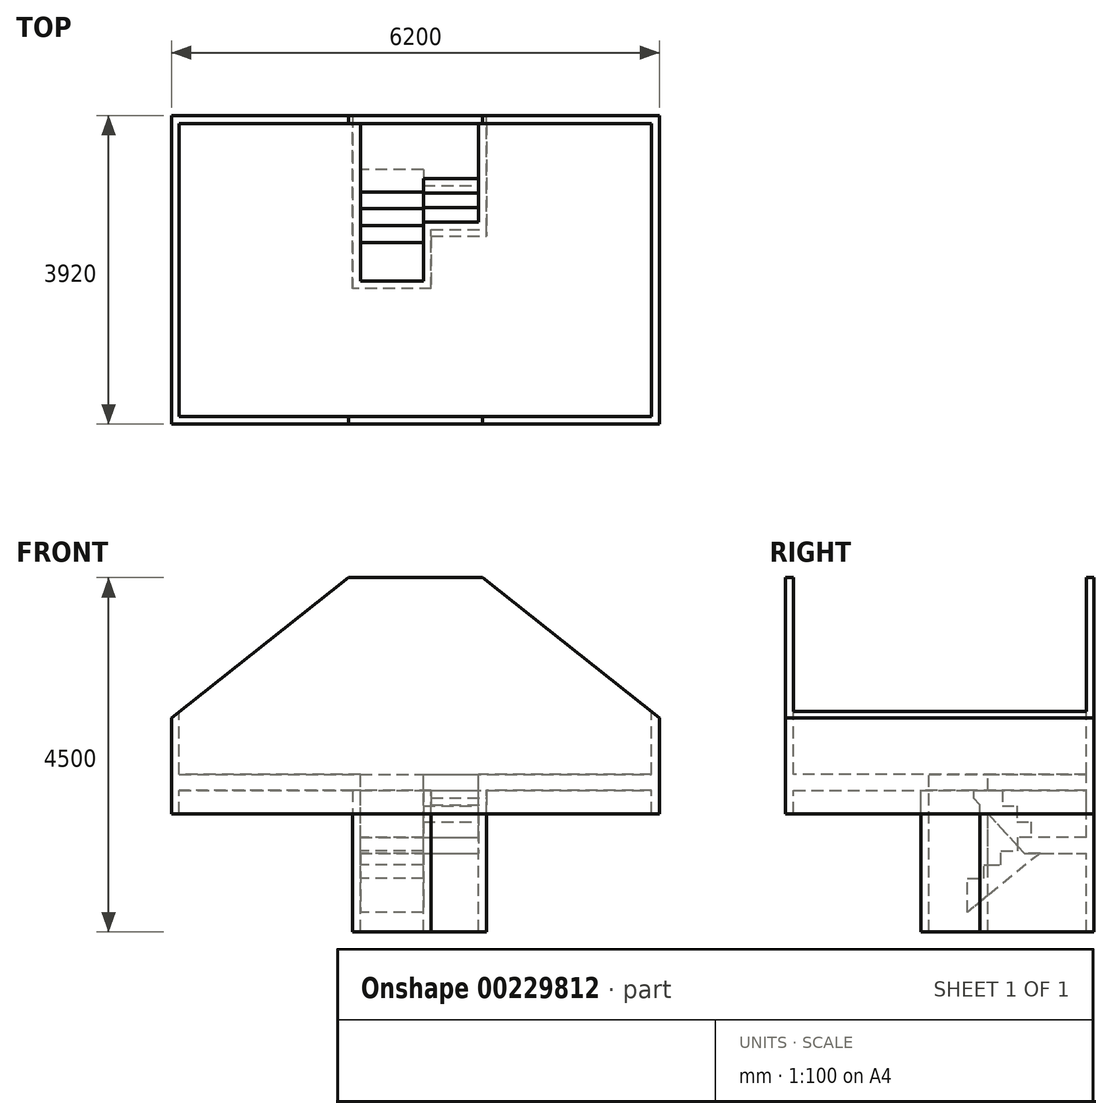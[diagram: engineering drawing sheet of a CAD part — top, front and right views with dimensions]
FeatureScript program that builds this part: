
annotation { "Feature Type Name" : "Feature", "Feature Type Description" : "" }
export const myFeature = defineFeature(function(context is Context, id is Id, definition is map)
    precondition{}
    {
        {
            var Q0;
            Q0=qCreatedBy(makeId("Top.planeOp"),FACE);
            var sketch = newSketch(context, id + "F0", { "sketchPlane" : qUnion([Q0])});
            skLineSegment(sketch, "E0.bottom", {"start": v(0, 0) * mm, "end": v(6000, 0) * mm});
            skLineSegment(sketch, "E0.top", {"start": v(0, -3720) * mm, "end": v(6000, -3720) * mm});
            skLineSegment(sketch, "E0.left", {"start": v(0, 0) * mm, "end": v(0, -3720) * mm});
            skLineSegment(sketch, "E0.right", {"start": v(6000, 0) * mm, "end": v(6000, -3720) * mm});
            skLineSegment(sketch, "E1", {"start": v(2300, 0) * mm, "end": v(2300, -2000) * mm});
            skLineSegment(sketch, "E2", {"start": v(2300, -2000) * mm, "end": v(3100, -2000) * mm});
            skLineSegment(sketch, "E3", {"start": v(3100, -2000) * mm, "end": v(3100, -1250) * mm});
            skLineSegment(sketch, "E4", {"start": v(3100, -1250) * mm, "end": v(3800, -1250) * mm});
            skLineSegment(sketch, "E5", {"start": v(3800, -1250) * mm, "end": v(3800, 0) * mm});
            skSolve(sketch);
        }
        {
            var Q0;
            Q0=qCreatedBy(makeId("Front.planeOp"),FACE);
            var sketch = newSketch(context, id + "F1", { "sketchPlane" : qUnion([Q0])});
            skLineSegment(sketch, "E6", {"start": v(0, 0) * mm, "end": v(0, 800) * mm});
            skLineSegment(sketch, "E7", {"start": v(0, 800) * mm, "end": v(2150, 2500) * mm});
            skLineSegment(sketch, "E8", {"start": v(2150, 2500) * mm, "end": v(3850, 2500) * mm});
            skPoint(sketch, "E9.end.orphan", {"position": v(5620.08, 0) * mm});
            skLineSegment(sketch, "E10.0", {"start": v(0, 0) * mm, "end": v(6000, 0) * mm});
            skLineSegment(sketch, "E11", {"start": v(6000, 0) * mm, "end": v(6000, 800) * mm});
            skLineSegment(sketch, "E12", {"start": v(6000, 800) * mm, "end": v(3850, 2500) * mm});
            skSolve(sketch);
        }
        {
            var Q0;
            Q0 = qSketchRegion(id + "F1", true);
            var sketch = newSketch(context, id + "F2", { "sketchPlane" : qUnion([Q0])});
            skSolve(sketch);
        }
        {
            var Q0;
            Q0=makeQuery(id+"F2.imprint","IMPRINT",FACE,{"disambiguationData":[TD([[makeQuery(id+"F2.imprint","IMPRINT",EDGE,{"derivedFrom":makeQuery(id+"F1.imprint","IMPRINT",EDGE,{"derivedFrom":sQuery(id+"F1.wireOp",EDGE,"E6")})}),-1.0]])]});
            var Q1;
            Q1=sQuery(id+"F0.wireOp",VERTEX,"E0.right.end");
            extrude(context, id + "F3", {"entities" : qUnion([Q0]), "endBound" : BoundingType.UP_TO_VERTEX, "endBoundEntityVertex" : qUnion([Q1]), "depth" : 25 * mm});
        }
        {
            var Q0;
            Q0=makeQuery(id+"F3.opExtrude","SWEPT_FACE",FACE,{"disambiguationData":[OSD([sQuery(id+"F1.wireOp",EDGE,"E12")])]});
            var Q1;
            Q1=makeQuery(id+"F3.opExtrude","SWEPT_FACE",FACE,{"disambiguationData":[OSD([sQuery(id+"F1.wireOp",EDGE,"E8")])]});
            var Q2;
            Q2=makeQuery(id+"F3.opExtrude","SWEPT_FACE",FACE,{"disambiguationData":[OSD([sQuery(id+"F1.wireOp",EDGE,"E7")])]});
            var Q3;
            Q3=makeQuery(id+"F3.opExtrude","SWEPT_FACE",FACE,{"disambiguationData":[OSD([sQuery(id+"F1.wireOp",EDGE,"E10.0")])]});
            var Q4;
            Q4=makeQuery(id+"F3.opExtrude","SWEPT_BODY",BODY,{"disambiguationData":[OSD([sQuery(id+"F1.wireOp",EDGE,"E6"),sQuery(id+"F1.wireOp",EDGE,"E7"),sQuery(id+"F1.wireOp",EDGE,"E8"),sQuery(id+"F1.wireOp",EDGE,"E10.0"),sQuery(id+"F1.wireOp",EDGE,"E11"),sQuery(id+"F1.wireOp",EDGE,"E12")])]});
            shell(context, id + "F4", {"entities" : qUnion([Q0, Q1, Q2, Q3]), "parts" : qUnion([Q4]), "thickness" : 100 * mm, "oppositeDirection" : true});
        }
        {
            var Q0;
            Q0=makeQuery(id+"F3.opExtrude","SWEPT_FACE",FACE,{"disambiguationData":[OSD([sQuery(id+"F1.wireOp",EDGE,"E10.0")])]});
            extrude(context, id + "F5", {"entities" : qUnion([Q0]), "operationType" : NewBodyOperationType.ADD, "depth" : 500 * mm});
        }
        {
            var Q0;
            Q0=qCreatedBy(makeId("Top.planeOp"),FACE);
            var sketch = newSketch(context, id + "F6", { "sketchPlane" : qUnion([Q0])});
            skLineSegment(sketch, "E13.0.0", {"start": v(3100, -1250) * mm, "end": v(3800, -1250) * mm});
            skLineSegment(sketch, "E13.0.1", {"start": v(3800, -1250) * mm, "end": v(3800, 0) * mm});
            skLineSegment(sketch, "E13.0.2", {"start": v(3800, 0) * mm, "end": v(2300, 0) * mm});
            skLineSegment(sketch, "E13.0.3", {"start": v(2300, 0) * mm, "end": v(2300, -2000) * mm});
            skLineSegment(sketch, "E13.0.4", {"start": v(2300, -2000) * mm, "end": v(3100, -2000) * mm});
            skLineSegment(sketch, "E13.0.5", {"start": v(3100, -2000) * mm, "end": v(3100, -1250) * mm});
            skLineSegment(sketch, "E14.0", {"start": v(2200, 100) * mm, "end": v(2200, -2100) * mm});
            skLineSegment(sketch, "E14.1", {"start": v(3200, -2100) * mm, "end": v(3200, -1350) * mm});
            skLineSegment(sketch, "E14.2", {"start": v(3200, -1350) * mm, "end": v(3900, -1350) * mm});
            skLineSegment(sketch, "E14.3", {"start": v(2200, -2100) * mm, "end": v(3200, -2100) * mm});
            skLineSegment(sketch, "E14.4", {"start": v(3900, -1350) * mm, "end": v(3900, 100) * mm});
            skLineSegment(sketch, "E14.5", {"start": v(3900, 100) * mm, "end": v(2200, 100) * mm});
            skSolve(sketch);
        }
        {
            var Q0;
            Q0 = qSketchRegion(id + "F6", true);
            extrude(context, id + "F7", {"entities" : qUnion([Q0]), "operationType" : NewBodyOperationType.ADD, "oppositeDirection" : true, "depth" : 2000 * mm});
        }
        {
            var Q0;
            Q0=qCreatedBy(makeId("Top.planeOp"),FACE);
            var sketch = newSketch(context, id + "F8", { "sketchPlane" : qUnion([Q0])});
            skLineSegment(sketch, "E15.0.0", {"start": v(3100, -1250) * mm, "end": v(3800, -1250) * mm});
            skLineSegment(sketch, "E15.0.1", {"start": v(3800, -1250) * mm, "end": v(3800, 0) * mm});
            skLineSegment(sketch, "E15.0.3", {"start": v(2300, 0) * mm, "end": v(2300, -2000) * mm});
            skLineSegment(sketch, "E15.0.4", {"start": v(2300, -2000) * mm, "end": v(3100, -2000) * mm});
            skLineSegment(sketch, "E15.0.5", {"start": v(3100, -2000) * mm, "end": v(3100, -1250) * mm});
            skLineSegment(sketch, "E16.0.5", {"start": v(2300, 0) * mm, "end": v(0, 0) * mm});
            skLineSegment(sketch, "E16.0.6", {"start": v(0, 0) * mm, "end": v(0, -3720) * mm});
            skLineSegment(sketch, "E16.0.7", {"start": v(0, -3720) * mm, "end": v(6000, -3720) * mm});
            skLineSegment(sketch, "E16.0.8", {"start": v(6000, -3720) * mm, "end": v(6000, 0) * mm});
            skLineSegment(sketch, "E16.0.9", {"start": v(6000, 0) * mm, "end": v(3800, 0) * mm});
            skSolve(sketch);
        }
        {
            var Q0;
            Q0 = qSketchRegion(id + "F8", true);
            extrude(context, id + "F9", {"entities" : qUnion([Q0]), "operationType" : NewBodyOperationType.ADD, "oppositeDirection" : true, "depth" : 200 * mm});
        }
        {
            var Q0;
            Q0=makeQuery(id+"F7.opExtrude","SWEPT_FACE",FACE,{"disambiguationData":[OSD([sQuery(id+"F6.wireOp",EDGE,"E14.4")])]});
            var sketch = newSketch(context, id + "F10", { "sketchPlane" : qUnion([Q0])});
            skLineSegment(sketch, "E17", {"start": v(0, -800) * mm, "end": v(-516.67, -800) * mm});
            skLineSegment(sketch, "E18", {"start": v(-700, -800) * mm, "end": v(-700, -600) * mm});
            skLineSegment(sketch, "E19", {"start": v(-700, -600) * mm, "end": v(-883.33, -600) * mm});
            skLineSegment(sketch, "E20", {"start": v(-883.33, -600) * mm, "end": v(-883.33, -400) * mm});
            skLineSegment(sketch, "E21", {"start": v(-883.33, -400) * mm, "end": v(-1066.67, -400) * mm});
            skLineSegment(sketch, "E22", {"start": v(-1066.67, -400) * mm, "end": v(-1066.67, -200) * mm});
            skLineSegment(sketch, "E23", {"start": v(-1066.67, -200) * mm, "end": v(-1250, -200) * mm});
            skLineSegment(sketch, "E24", {"start": v(-1250, -200) * mm, "end": v(-1250, 0) * mm});
            skLineSegment(sketch, "E25.0", {"start": v(-1433.33, 0) * mm, "end": v(-1250, 0) * mm});
            skPoint(sketch, "E26.orphan", {"position": v(-246.26, 0) * mm});
            skPoint(sketch, "E27.orphan", {"position": v(-1433.5, -1048.96) * mm});
            skPoint(sketch, "E28.end.orphan", {"position": v(-1433.5, -800) * mm});
            skPoint(sketch, "E28.start.orphan", {"position": v(-1433.5, -924.48) * mm});
            skLineSegment(sketch, "E29", {"start": v(-700, -800) * mm, "end": v(-516.67, -800) * mm});
            skLineSegment(sketch, "E30", {"start": v(-1433.33, 0) * mm, "end": v(-1433.33, -295.98) * mm});
            skLineSegment(sketch, "E31", {"start": v(-1433.33, -295.98) * mm, "end": v(-787.98, -1000) * mm});
            skLineSegment(sketch, "E32", {"start": v(-787.98, -1000) * mm, "end": v(0, -1000) * mm});
            skPoint(sketch, "E32.endSnap0", {"position": v(0, -1000) * mm});
            skLineSegment(sketch, "E33", {"start": v(0, -1000) * mm, "end": v(0, -800) * mm});
            skLineSegment(sketch, "E34", {"start": v(-1250, -200) * mm, "end": v(-1066.67, -400) * mm, "construction": true});
            skLineSegment(sketch, "E35", {"start": v(-700, -800) * mm, "end": v(-847.43, -935.14) * mm, "construction": true});
            skPoint(sketch, "E36.orphan", {"position": v(-700, -1095.98) * mm});
            skPoint(sketch, "E37.orphan", {"position": v(-835.8, -924.48) * mm});
            skSolve(sketch);
        }
        {
            var Q0;
            Q0 = qSketchRegion(id + "F10", true);
            var Q1;
            Q1=makeQuery(id+"F7.opExtrude","SWEPT_FACE",FACE,{"disambiguationData":[OSD([sQuery(id+"F6.wireOp",EDGE,"E13.0.5")])]});
            extrude(context, id + "F11", {"entities" : qUnion([Q0]), "operationType" : NewBodyOperationType.ADD, "endBound" : BoundingType.UP_TO_SURFACE, "oppositeDirection" : true, "endBoundEntityFace" : qUnion([Q1]), "depth" : 25 * mm});
        }
        {
            var Q0;
            Q0=makeQuery(id+"F7.opExtrude","SWEPT_FACE",FACE,{"disambiguationData":[OSD([sQuery(id+"F6.wireOp",EDGE,"E14.0")])]});
            var sketch = newSketch(context, id + "F12", { "sketchPlane" : qUnion([Q0])});
            skLineSegment(sketch, "E38", {"start": v(1510.8, -1750.14) * mm, "end": v(1510.8, -1319.54) * mm});
            skLineSegment(sketch, "E39", {"start": v(1510.8, -1319.54) * mm, "end": v(1297.08, -1319.54) * mm});
            skLineSegment(sketch, "E40", {"start": v(1297.08, -1319.54) * mm, "end": v(1297.08, -1146.36) * mm});
            skLineSegment(sketch, "E41", {"start": v(1297.08, -1146.36) * mm, "end": v(1083.36, -1146.36) * mm});
            skLineSegment(sketch, "E42", {"start": v(1083.36, -1146.36) * mm, "end": v(1083.36, -973.18) * mm});
            skLineSegment(sketch, "E43", {"start": v(1083.36, -973.18) * mm, "end": v(869.64, -973.18) * mm});
            skLineSegment(sketch, "E44", {"start": v(585.06, -1000) * mm, "end": v(1510.8, -1750.14) * mm});
            skLineSegment(sketch, "E45", {"start": v(869.64, -973.18) * mm, "end": v(1083.36, -1146.36) * mm, "construction": true});
            skLineSegment(sketch, "E46.0", {"start": v(585.06, -1000) * mm, "end": v(0, -1000) * mm});
            skLineSegment(sketch, "E46.1", {"start": v(0, -1000) * mm, "end": v(0, -800) * mm});
            skLineSegment(sketch, "E46.2", {"start": v(0, -800) * mm, "end": v(869.64, -800) * mm});
            skLineSegment(sketch, "E46.3", {"start": v(869.64, -973.18) * mm, "end": v(869.64, -800) * mm});
            skPoint(sketch, "E47.orphan", {"position": v(869.64, -800) * mm});
            skPoint(sketch, "E48.orphan", {"position": v(508.8, -923.61) * mm});
            skSolve(sketch);
        }
        {
            var Q0;
            Q0 = qSketchRegion(id + "F12", true);
            var Q1;
            {var subQ0=sQuery(id+"F6.wireOp",EDGE,"E13.0.5");Q1=makeQuery(id+"F11.boolean.opBoolean","MERGE",FACE,{"derivedFrom":[makeQuery(id+"F7.opExtrude","SWEPT_FACE",FACE,{"disambiguationData":[OSD([subQ0])]}),makeQuery(id+"F11.opExtrude","CAP_FACE",FACE,{"disambiguationData":[OSD([subQ0])],"isStart":false})]});}
            extrude(context, id + "F13", {"entities" : qUnion([Q0]), "operationType" : NewBodyOperationType.ADD, "endBound" : BoundingType.UP_TO_SURFACE, "oppositeDirection" : true, "endBoundEntityFace" : qUnion([Q1]), "depth" : 25 * mm});
        }
    });
